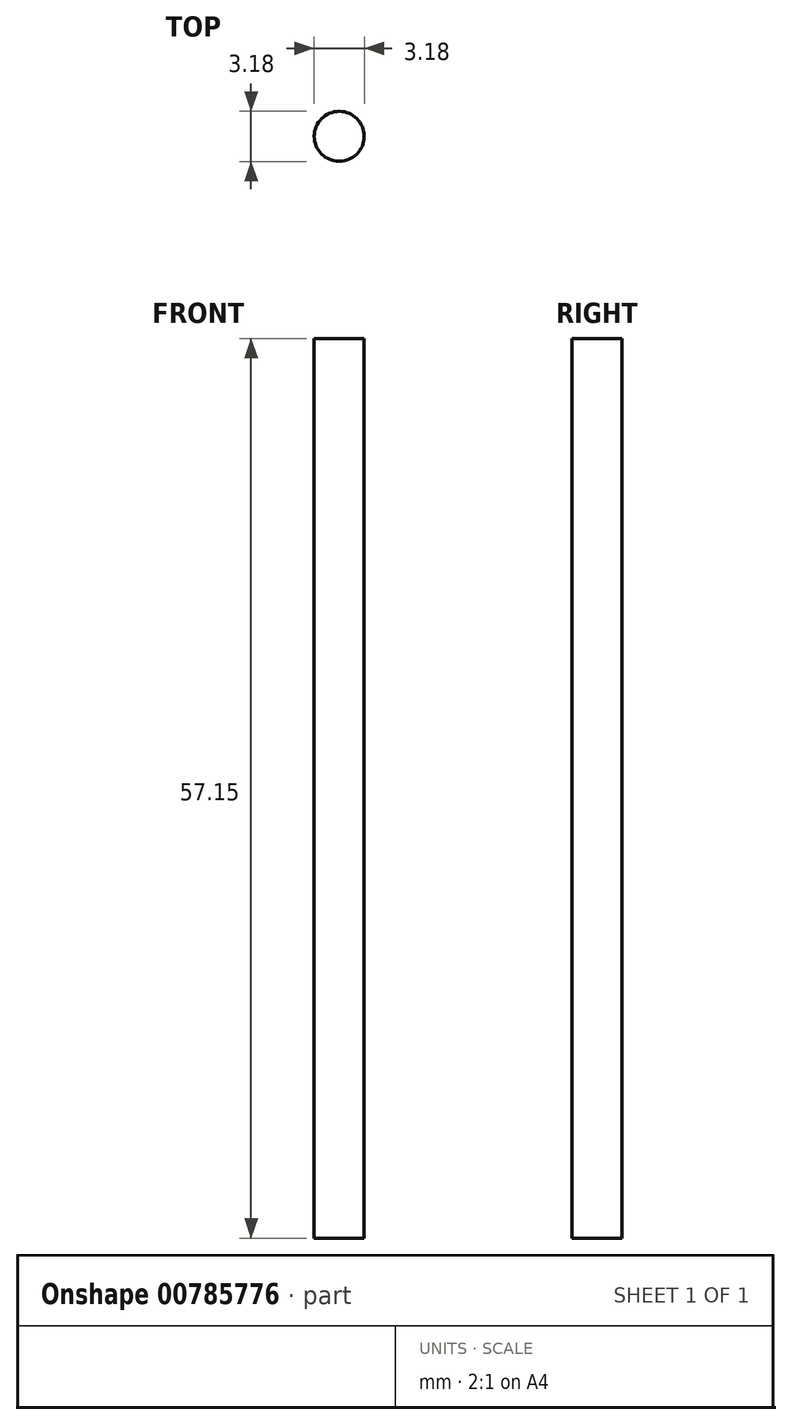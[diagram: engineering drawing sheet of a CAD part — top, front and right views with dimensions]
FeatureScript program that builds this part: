
annotation { "Feature Type Name" : "Feature", "Feature Type Description" : "" }
export const myFeature = defineFeature(function(context is Context, id is Id, definition is map)
    precondition{}
    {
        {
            var Q0;
            Q0=qCreatedBy(makeId("Top.planeOp"),FACE);
            var sketch = newSketch(context, id + "F0", { "sketchPlane" : qUnion([Q0])});
            skCircle(sketch, "E0", {"center": v(0, 0) * mm, "radius": 1.59 * mm});
            skSolve(sketch);
        }
        {
            var Q0;
            Q0=qSketchRegion(id+"F0",true);
            extrude(context, id + "F1", {"entities" : qUnion([Q0]), "depth" : 57.15 * mm, "offsetDistance" : 25.4 * mm});
        }
    });
